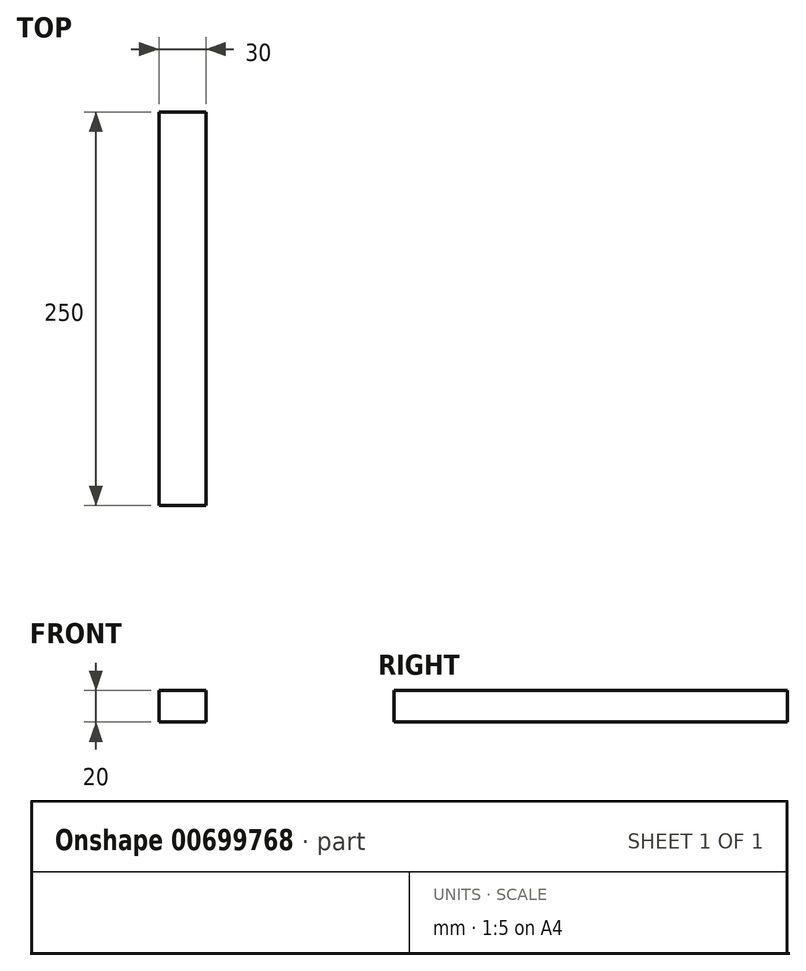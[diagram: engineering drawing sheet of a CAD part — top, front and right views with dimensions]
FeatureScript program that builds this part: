
annotation { "Feature Type Name" : "Feature", "Feature Type Description" : "" }
export const myFeature = defineFeature(function(context is Context, id is Id, definition is map)
    precondition{}
    {
        {
            var Q0;
            Q0=qCreatedBy(makeId("Top.planeOp"),FACE);
            var sketch = newSketch(context, id + "F0", { "sketchPlane" : qUnion([Q0])});
            skLineSegment(sketch, "E0.bottom", {"start": v(-15, 125) * mm, "end": v(15, 125) * mm});
            skLineSegment(sketch, "E0.top", {"start": v(-15, -125) * mm, "end": v(15, -125) * mm});
            skLineSegment(sketch, "E0.left", {"start": v(-15, 125) * mm, "end": v(-15, -125) * mm});
            skLineSegment(sketch, "E0.right", {"start": v(15, 125) * mm, "end": v(15, -125) * mm});
            skPoint(sketch, "E0.middle", {"position": v(0, 0) * mm});
            skSolve(sketch);
        }
        {
            var Q0;
            Q0=makeQuery(id+"F0.imprint","IMPRINT",FACE,{"disambiguationData":[TD([[makeQuery(id+"F0.imprint","IMPRINT",EDGE,{"derivedFrom":sQuery(id+"F0.wireOp",EDGE,"E0.bottom")}),-1.0]])]});
            extrude(context, id + "F1", {"entities" : qUnion([Q0]), "depth" : 20 * mm, "offsetDistance" : 25 * mm});
        }
    });
